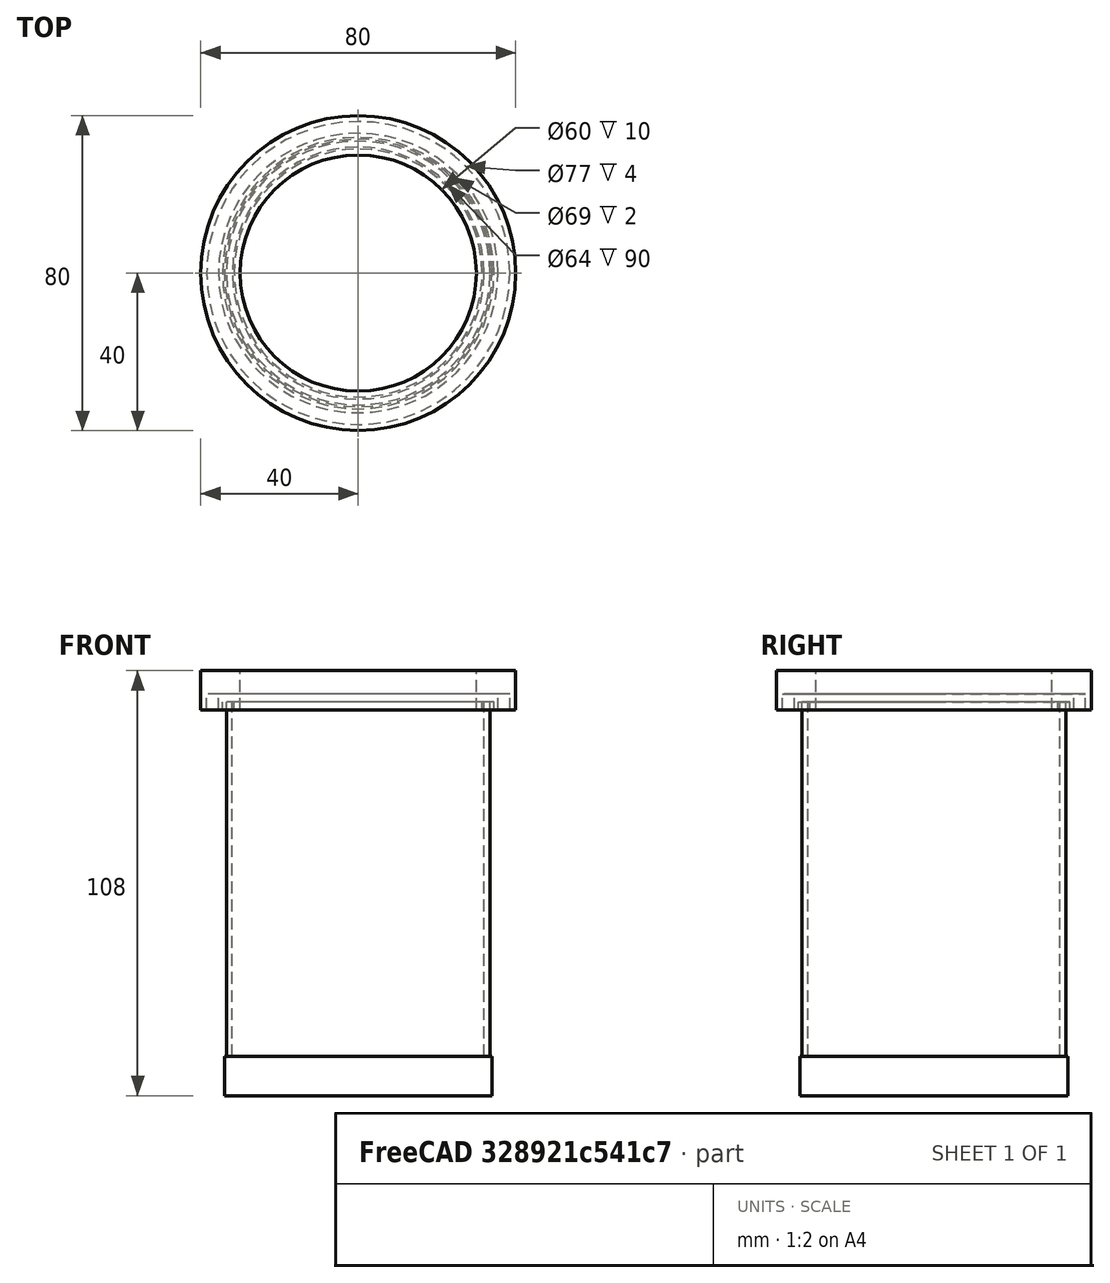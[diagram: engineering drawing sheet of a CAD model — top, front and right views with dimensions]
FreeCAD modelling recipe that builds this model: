
FCSTD DOCUMENT  (FreeCAD 0.19R24267 +99 (Git))
Label: basura
License: All rights reserved
LicenseURL: http://en.wikipedia.org/wiki/All_rights_reserved
objects: Part::FeaturePython×4, Part::Cut×2, Part::Cylinder×1, Part::MultiFuse×1
note: 8 computed .brp shape members not serialized (recipe doc carries the construction recipe); baked Part::Feature solids carry a one-line shape summary decoded from their .brp

FEATURE [Part::FeaturePython] Tube  # WARN: FeaturePython — macro-defined, semantics opaque (R4)
  AttacherType = Attacher::AttachEngine3D
  Height = 100
  InnerRadius = 32
  OuterRadius = 33.5
FEATURE [Part::Cylinder] Cylinder  label="Cilindro"
  Angle = 360
  AttacherType = Attacher::AttachEngine3D
  Height = 10
  Radius = 34
FEATURE [Part::MultiFuse] Fusion  label="basura 34mmR"
  Shapes = -> [Tube,Cylinder]
FEATURE [Part::FeaturePython] Tube001  # WARN: FeaturePython — macro-defined, semantics opaque (R4)
  AttacherType = Attacher::AttachEngine3D
  Height = 10
  InnerRadius = 30
  OuterRadius = 40
  Placement = pos=(0,0,98) rot=(0,0,1;0rad)
FEATURE [Part::FeaturePython] Tube002  # WARN: FeaturePython — macro-defined, semantics opaque (R4)
  AttacherType = Attacher::AttachEngine3D
  Height = 100
  InnerRadius = 31.5
  OuterRadius = 34.5
FEATURE [Part::Cut] Cut
  Base = -> Tube001
  Tool = -> Tube002
FEATURE [Part::FeaturePython] Tube003  # WARN: FeaturePython — macro-defined, semantics opaque (R4)
  AttacherType = Attacher::AttachEngine3D
  Height = 10
  InnerRadius = 35.5
  OuterRadius = 38.5
  Placement = pos=(0,0,92) rot=(0,0,1;0rad)
FEATURE [Part::Cut] Cut001
  Base = -> Cut
  Tool = -> Tube003
